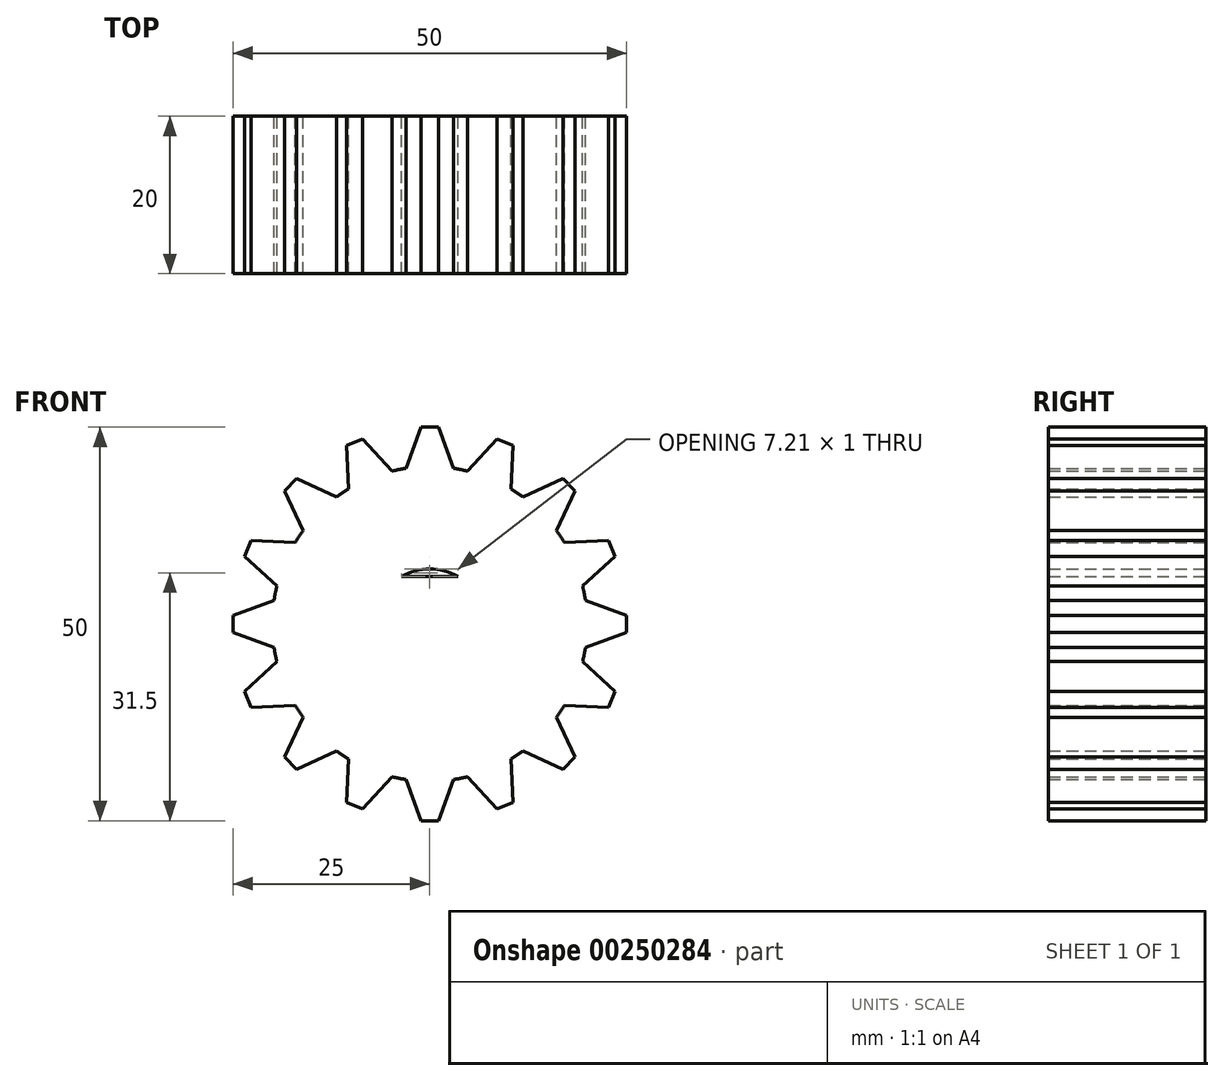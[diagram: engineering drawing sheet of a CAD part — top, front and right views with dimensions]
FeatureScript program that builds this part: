
annotation { "Feature Type Name" : "Feature", "Feature Type Description" : "" }
export const myFeature = defineFeature(function(context is Context, id is Id, definition is map)
    precondition{}
    {
        {
            var Q0;
            Q0=qCreatedBy(makeId("Front.planeOp"),FACE);
            var sketch = newSketch(context, id + "F0", { "sketchPlane" : qUnion([Q0])});
            skCircle(sketch, "E0", {"center": v(0, 0) * mm, "radius": 20 * mm});
            skPoint(sketch, "E1", {"position": v(0, 20) * mm});
            skLineSegment(sketch, "E2", {"start": v(0, 20) * mm, "end": v(0, 30) * mm, "construction": true});
            skPoint(sketch, "E3", {"position": v(0, 25) * mm});
            skLineSegment(sketch, "E4", {"start": v(-1.1, 25) * mm, "end": v(1.1, 25) * mm});
            skLineSegment(sketch, "E5", {"start": v(1.1, 25) * mm, "end": v(3, 19.77) * mm});
            skLineSegment(sketch, "E6", {"start": v(-1.1, 25) * mm, "end": v(-3, 19.77) * mm});
            skLineSegment(sketch, "E7", {"start": v(-3, 19.77) * mm, "end": v(3, 19.77) * mm});
            skLineSegment(sketch, "E8.1.0", {"start": v(-8.55, 23.52) * mm, "end": v(-4.8, 19.42) * mm});
            skLineSegment(sketch, "E8.1.1", {"start": v(-10.58, 22.68) * mm, "end": v(-10.34, 17.12) * mm});
            skPoint(sketch, "E8.1.2", {"position": v(-9.57, 23.1) * mm});
            skLineSegment(sketch, "E8.1.3", {"start": v(-10.34, 17.12) * mm, "end": v(-4.8, 19.42) * mm});
            skLineSegment(sketch, "E8.1.4", {"start": v(-7.65, 18.48) * mm, "end": v(-11.48, 27.72) * mm, "construction": true});
            skPoint(sketch, "E8.1.5", {"position": v(-7.65, 18.48) * mm});
            skLineSegment(sketch, "E8.1.6", {"start": v(-10.58, 22.68) * mm, "end": v(-8.55, 23.52) * mm});
            skLineSegment(sketch, "E8.2.0", {"start": v(-16.9, 18.45) * mm, "end": v(-11.86, 16.1) * mm});
            skLineSegment(sketch, "E8.2.1", {"start": v(-18.45, 16.9) * mm, "end": v(-16.1, 11.86) * mm});
            skPoint(sketch, "E8.2.2", {"position": v(-17.68, 17.68) * mm});
            skLineSegment(sketch, "E8.2.3", {"start": v(-16.1, 11.86) * mm, "end": v(-11.86, 16.1) * mm});
            skLineSegment(sketch, "E8.2.4", {"start": v(-14.14, 14.14) * mm, "end": v(-21.21, 21.21) * mm, "construction": true});
            skPoint(sketch, "E8.2.5", {"position": v(-14.14, 14.14) * mm});
            skLineSegment(sketch, "E8.2.6", {"start": v(-18.45, 16.9) * mm, "end": v(-16.9, 18.45) * mm});
            skLineSegment(sketch, "E8.3.0", {"start": v(-22.68, 10.58) * mm, "end": v(-17.12, 10.34) * mm});
            skLineSegment(sketch, "E8.3.1", {"start": v(-23.52, 8.55) * mm, "end": v(-19.42, 4.8) * mm});
            skPoint(sketch, "E8.3.2", {"position": v(-23.1, 9.57) * mm});
            skLineSegment(sketch, "E8.3.3", {"start": v(-19.42, 4.8) * mm, "end": v(-17.12, 10.34) * mm});
            skLineSegment(sketch, "E8.3.4", {"start": v(-18.48, 7.65) * mm, "end": v(-27.72, 11.48) * mm, "construction": true});
            skPoint(sketch, "E8.3.5", {"position": v(-18.48, 7.65) * mm});
            skLineSegment(sketch, "E8.3.6", {"start": v(-23.52, 8.55) * mm, "end": v(-22.68, 10.58) * mm});
            skLineSegment(sketch, "E8.4.0", {"start": v(-25, 1.1) * mm, "end": v(-19.77, 3) * mm});
            skLineSegment(sketch, "E8.4.1", {"start": v(-25, -1.1) * mm, "end": v(-19.77, -3) * mm});
            skPoint(sketch, "E8.4.2", {"position": v(-25, 0) * mm});
            skLineSegment(sketch, "E8.4.3", {"start": v(-19.77, -3) * mm, "end": v(-19.77, 3) * mm});
            skLineSegment(sketch, "E8.4.4", {"start": v(-20, 0) * mm, "end": v(-30, 0) * mm, "construction": true});
            skPoint(sketch, "E8.4.5", {"position": v(-20, 0) * mm});
            skLineSegment(sketch, "E8.4.6", {"start": v(-25, -1.1) * mm, "end": v(-25, 1.1) * mm});
            skLineSegment(sketch, "E8.5.0", {"start": v(-23.52, -8.55) * mm, "end": v(-19.42, -4.8) * mm});
            skLineSegment(sketch, "E8.5.1", {"start": v(-22.68, -10.58) * mm, "end": v(-17.12, -10.34) * mm});
            skPoint(sketch, "E8.5.2", {"position": v(-23.1, -9.57) * mm});
            skLineSegment(sketch, "E8.5.3", {"start": v(-17.12, -10.34) * mm, "end": v(-19.42, -4.8) * mm});
            skLineSegment(sketch, "E8.5.4", {"start": v(-18.48, -7.65) * mm, "end": v(-27.72, -11.48) * mm, "construction": true});
            skPoint(sketch, "E8.5.5", {"position": v(-18.48, -7.65) * mm});
            skLineSegment(sketch, "E8.5.6", {"start": v(-22.68, -10.58) * mm, "end": v(-23.52, -8.55) * mm});
            skLineSegment(sketch, "E8.6.0", {"start": v(-18.45, -16.9) * mm, "end": v(-16.1, -11.86) * mm});
            skLineSegment(sketch, "E8.6.1", {"start": v(-16.9, -18.45) * mm, "end": v(-11.86, -16.1) * mm});
            skPoint(sketch, "E8.6.2", {"position": v(-17.68, -17.68) * mm});
            skLineSegment(sketch, "E8.6.3", {"start": v(-11.86, -16.1) * mm, "end": v(-16.1, -11.86) * mm});
            skLineSegment(sketch, "E8.6.4", {"start": v(-14.14, -14.14) * mm, "end": v(-21.21, -21.21) * mm, "construction": true});
            skPoint(sketch, "E8.6.5", {"position": v(-14.14, -14.14) * mm});
            skLineSegment(sketch, "E8.6.6", {"start": v(-16.9, -18.45) * mm, "end": v(-18.45, -16.9) * mm});
            skLineSegment(sketch, "E8.7.0", {"start": v(-10.58, -22.68) * mm, "end": v(-10.34, -17.12) * mm});
            skLineSegment(sketch, "E8.7.1", {"start": v(-8.55, -23.52) * mm, "end": v(-4.8, -19.42) * mm});
            skPoint(sketch, "E8.7.2", {"position": v(-9.57, -23.1) * mm});
            skLineSegment(sketch, "E8.7.3", {"start": v(-4.8, -19.42) * mm, "end": v(-10.34, -17.12) * mm});
            skLineSegment(sketch, "E8.7.4", {"start": v(-7.65, -18.48) * mm, "end": v(-11.48, -27.72) * mm, "construction": true});
            skPoint(sketch, "E8.7.5", {"position": v(-7.65, -18.48) * mm});
            skLineSegment(sketch, "E8.7.6", {"start": v(-8.55, -23.52) * mm, "end": v(-10.58, -22.68) * mm});
            skLineSegment(sketch, "E8.8.0", {"start": v(-1.1, -25) * mm, "end": v(-3, -19.77) * mm});
            skLineSegment(sketch, "E8.8.1", {"start": v(1.1, -25) * mm, "end": v(3, -19.77) * mm});
            skPoint(sketch, "E8.8.2", {"position": v(0, -25) * mm});
            skLineSegment(sketch, "E8.8.3", {"start": v(3, -19.77) * mm, "end": v(-3, -19.77) * mm});
            skLineSegment(sketch, "E8.8.4", {"start": v(0, -20) * mm, "end": v(0, -30) * mm, "construction": true});
            skPoint(sketch, "E8.8.5", {"position": v(0, -20) * mm});
            skLineSegment(sketch, "E8.8.6", {"start": v(1.1, -25) * mm, "end": v(-1.1, -25) * mm});
            skLineSegment(sketch, "E8.9.0", {"start": v(8.55, -23.52) * mm, "end": v(4.8, -19.42) * mm});
            skLineSegment(sketch, "E8.9.1", {"start": v(10.58, -22.68) * mm, "end": v(10.34, -17.12) * mm});
            skPoint(sketch, "E8.9.2", {"position": v(9.57, -23.1) * mm});
            skLineSegment(sketch, "E8.9.3", {"start": v(10.34, -17.12) * mm, "end": v(4.8, -19.42) * mm});
            skLineSegment(sketch, "E8.9.4", {"start": v(7.65, -18.48) * mm, "end": v(11.48, -27.72) * mm, "construction": true});
            skPoint(sketch, "E8.9.5", {"position": v(7.65, -18.48) * mm});
            skLineSegment(sketch, "E8.9.6", {"start": v(10.58, -22.68) * mm, "end": v(8.55, -23.52) * mm});
            skLineSegment(sketch, "E8.10.0", {"start": v(16.9, -18.45) * mm, "end": v(11.86, -16.1) * mm});
            skLineSegment(sketch, "E8.10.1", {"start": v(18.45, -16.9) * mm, "end": v(16.1, -11.86) * mm});
            skPoint(sketch, "E8.10.2", {"position": v(17.68, -17.68) * mm});
            skLineSegment(sketch, "E8.10.3", {"start": v(16.1, -11.86) * mm, "end": v(11.86, -16.1) * mm});
            skLineSegment(sketch, "E8.10.4", {"start": v(14.14, -14.14) * mm, "end": v(21.21, -21.21) * mm, "construction": true});
            skPoint(sketch, "E8.10.5", {"position": v(14.14, -14.14) * mm});
            skLineSegment(sketch, "E8.10.6", {"start": v(18.45, -16.9) * mm, "end": v(16.9, -18.45) * mm});
            skLineSegment(sketch, "E8.11.0", {"start": v(22.68, -10.58) * mm, "end": v(17.12, -10.34) * mm});
            skLineSegment(sketch, "E8.11.1", {"start": v(23.52, -8.55) * mm, "end": v(19.42, -4.8) * mm});
            skPoint(sketch, "E8.11.2", {"position": v(23.1, -9.57) * mm});
            skLineSegment(sketch, "E8.11.3", {"start": v(19.42, -4.8) * mm, "end": v(17.12, -10.34) * mm});
            skLineSegment(sketch, "E8.11.4", {"start": v(18.48, -7.65) * mm, "end": v(27.72, -11.48) * mm, "construction": true});
            skPoint(sketch, "E8.11.5", {"position": v(18.48, -7.65) * mm});
            skLineSegment(sketch, "E8.11.6", {"start": v(23.52, -8.55) * mm, "end": v(22.68, -10.58) * mm});
            skLineSegment(sketch, "E8.12.0", {"start": v(25, -1.1) * mm, "end": v(19.77, -3) * mm});
            skLineSegment(sketch, "E8.12.1", {"start": v(25, 1.1) * mm, "end": v(19.77, 3) * mm});
            skPoint(sketch, "E8.12.2", {"position": v(25, 0) * mm});
            skLineSegment(sketch, "E8.12.3", {"start": v(19.77, 3) * mm, "end": v(19.77, -3) * mm});
            skLineSegment(sketch, "E8.12.4", {"start": v(20, 0) * mm, "end": v(30, 0) * mm, "construction": true});
            skPoint(sketch, "E8.12.5", {"position": v(20, 0) * mm});
            skLineSegment(sketch, "E8.12.6", {"start": v(25, 1.1) * mm, "end": v(25, -1.1) * mm});
            skLineSegment(sketch, "E8.13.0", {"start": v(23.52, 8.55) * mm, "end": v(19.42, 4.8) * mm});
            skLineSegment(sketch, "E8.13.1", {"start": v(22.68, 10.58) * mm, "end": v(17.12, 10.34) * mm});
            skPoint(sketch, "E8.13.2", {"position": v(23.1, 9.57) * mm});
            skLineSegment(sketch, "E8.13.3", {"start": v(17.12, 10.34) * mm, "end": v(19.42, 4.8) * mm});
            skLineSegment(sketch, "E8.13.4", {"start": v(18.48, 7.65) * mm, "end": v(27.72, 11.48) * mm, "construction": true});
            skPoint(sketch, "E8.13.5", {"position": v(18.48, 7.65) * mm});
            skLineSegment(sketch, "E8.13.6", {"start": v(22.68, 10.58) * mm, "end": v(23.52, 8.55) * mm});
            skLineSegment(sketch, "E8.14.0", {"start": v(18.45, 16.9) * mm, "end": v(16.1, 11.86) * mm});
            skLineSegment(sketch, "E8.14.1", {"start": v(16.9, 18.45) * mm, "end": v(11.86, 16.1) * mm});
            skPoint(sketch, "E8.14.2", {"position": v(17.68, 17.68) * mm});
            skLineSegment(sketch, "E8.14.3", {"start": v(11.86, 16.1) * mm, "end": v(16.1, 11.86) * mm});
            skLineSegment(sketch, "E8.14.4", {"start": v(14.14, 14.14) * mm, "end": v(21.21, 21.21) * mm, "construction": true});
            skPoint(sketch, "E8.14.5", {"position": v(14.14, 14.14) * mm});
            skLineSegment(sketch, "E8.14.6", {"start": v(16.9, 18.45) * mm, "end": v(18.45, 16.9) * mm});
            skLineSegment(sketch, "E8.15.0", {"start": v(10.58, 22.68) * mm, "end": v(10.34, 17.12) * mm});
            skLineSegment(sketch, "E8.15.1", {"start": v(8.55, 23.52) * mm, "end": v(4.8, 19.42) * mm});
            skPoint(sketch, "E8.15.2", {"position": v(9.57, 23.1) * mm});
            skLineSegment(sketch, "E8.15.3", {"start": v(4.8, 19.42) * mm, "end": v(10.34, 17.12) * mm});
            skLineSegment(sketch, "E8.15.4", {"start": v(7.65, 18.48) * mm, "end": v(11.48, 27.72) * mm, "construction": true});
            skPoint(sketch, "E8.15.5", {"position": v(7.65, 18.48) * mm});
            skLineSegment(sketch, "E8.15.6", {"start": v(8.55, 23.52) * mm, "end": v(10.58, 22.68) * mm});
            skSolve(sketch);
        }
        {
            var Q0;
            Q0 = qSketchRegion(id + "F0", true);
            extrude(context, id + "F1", {"entities" : qUnion([Q0]), "depth" : 20 * mm});
        }
        {
            var Q0;
            Q0=makeQuery(id+"F1.opExtrude","CAP_FACE",FACE,{"disambiguationData":[OSD([sQuery(id+"F0.wireOp",EDGE,"E4"),sQuery(id+"F0.wireOp",EDGE,"E5"),sQuery(id+"F0.wireOp",EDGE,"E6"),sQuery(id+"F0.wireOp",EDGE,"17c51863-979c-42ed-b14d-551197cb4550.1.4"),sQuery(id+"F0.wireOp",EDGE,"17c51863-979c-42ed-b14d-551197cb4550.1.5"),sQuery(id+"F0.wireOp",EDGE,"17c51863-979c-42ed-b14d-551197cb4550.1.6"),sQuery(id+"F0.wireOp",EDGE,"17c51863-979c-42ed-b14d-551197cb4550.2.4"),sQuery(id+"F0.wireOp",EDGE,"17c51863-979c-42ed-b14d-551197cb4550.2.5"),sQuery(id+"F0.wireOp",EDGE,"17c51863-979c-42ed-b14d-551197cb4550.2.6"),sQuery(id+"F0.wireOp",EDGE,"17c51863-979c-42ed-b14d-551197cb4550.3.4"),sQuery(id+"F0.wireOp",EDGE,"17c51863-979c-42ed-b14d-551197cb4550.3.5"),sQuery(id+"F0.wireOp",EDGE,"17c51863-979c-42ed-b14d-551197cb4550.3.6"),sQuery(id+"F0.wireOp",EDGE,"17c51863-979c-42ed-b14d-551197cb4550.4.4"),sQuery(id+"F0.wireOp",EDGE,"17c51863-979c-42ed-b14d-551197cb4550.4.5"),sQuery(id+"F0.wireOp",EDGE,"17c51863-979c-42ed-b14d-551197cb4550.4.6"),sQuery(id+"F0.wireOp",EDGE,"17c51863-979c-42ed-b14d-551197cb4550.5.4"),sQuery(id+"F0.wireOp",EDGE,"17c51863-979c-42ed-b14d-551197cb4550.5.5"),sQuery(id+"F0.wireOp",EDGE,"17c51863-979c-42ed-b14d-551197cb4550.5.6"),sQuery(id+"F0.wireOp",EDGE,"17c51863-979c-42ed-b14d-551197cb4550.6.4"),sQuery(id+"F0.wireOp",EDGE,"17c51863-979c-42ed-b14d-551197cb4550.6.5"),sQuery(id+"F0.wireOp",EDGE,"17c51863-979c-42ed-b14d-551197cb4550.6.6"),sQuery(id+"F0.wireOp",EDGE,"17c51863-979c-42ed-b14d-551197cb4550.7.4"),sQuery(id+"F0.wireOp",EDGE,"17c51863-979c-42ed-b14d-551197cb4550.7.5"),sQuery(id+"F0.wireOp",EDGE,"17c51863-979c-42ed-b14d-551197cb4550.7.6"),sQuery(id+"F0.wireOp",EDGE,"17c51863-979c-42ed-b14d-551197cb4550.8.4"),sQuery(id+"F0.wireOp",EDGE,"17c51863-979c-42ed-b14d-551197cb4550.8.5"),sQuery(id+"F0.wireOp",EDGE,"17c51863-979c-42ed-b14d-551197cb4550.8.6"),sQuery(id+"F0.wireOp",EDGE,"17c51863-979c-42ed-b14d-551197cb4550.9.4"),sQuery(id+"F0.wireOp",EDGE,"17c51863-979c-42ed-b14d-551197cb4550.9.5"),sQuery(id+"F0.wireOp",EDGE,"17c51863-979c-42ed-b14d-551197cb4550.9.6"),sQuery(id+"F0.wireOp",EDGE,"17c51863-979c-42ed-b14d-551197cb4550.10.4"),sQuery(id+"F0.wireOp",EDGE,"17c51863-979c-42ed-b14d-551197cb4550.10.5"),sQuery(id+"F0.wireOp",EDGE,"17c51863-979c-42ed-b14d-551197cb4550.10.6"),sQuery(id+"F0.wireOp",EDGE,"17c51863-979c-42ed-b14d-551197cb4550.11.4"),sQuery(id+"F0.wireOp",EDGE,"17c51863-979c-42ed-b14d-551197cb4550.11.5"),sQuery(id+"F0.wireOp",EDGE,"17c51863-979c-42ed-b14d-551197cb4550.11.6"),sQuery(id+"F0.wireOp",EDGE,"17c51863-979c-42ed-b14d-551197cb4550.12.4"),sQuery(id+"F0.wireOp",EDGE,"17c51863-979c-42ed-b14d-551197cb4550.12.5"),sQuery(id+"F0.wireOp",EDGE,"17c51863-979c-42ed-b14d-551197cb4550.12.6"),sQuery(id+"F0.wireOp",EDGE,"17c51863-979c-42ed-b14d-551197cb4550.13.4"),sQuery(id+"F0.wireOp",EDGE,"17c51863-979c-42ed-b14d-551197cb4550.13.5"),sQuery(id+"F0.wireOp",EDGE,"17c51863-979c-42ed-b14d-551197cb4550.13.6"),sQuery(id+"F0.wireOp",EDGE,"17c51863-979c-42ed-b14d-551197cb4550.14.4"),sQuery(id+"F0.wireOp",EDGE,"17c51863-979c-42ed-b14d-551197cb4550.14.5"),sQuery(id+"F0.wireOp",EDGE,"17c51863-979c-42ed-b14d-551197cb4550.14.6"),sQuery(id+"F0.wireOp",EDGE,"17c51863-979c-42ed-b14d-551197cb4550.15.4"),sQuery(id+"F0.wireOp",EDGE,"17c51863-979c-42ed-b14d-551197cb4550.15.5"),sQuery(id+"F0.wireOp",EDGE,"17c51863-979c-42ed-b14d-551197cb4550.15.6"),sQuery(id+"F0.wireOp",EDGE,"17c51863-979c-42ed-b14d-551197cb4550.16.4"),sQuery(id+"F0.wireOp",EDGE,"17c51863-979c-42ed-b14d-551197cb4550.16.5"),sQuery(id+"F0.wireOp",EDGE,"17c51863-979c-42ed-b14d-551197cb4550.16.6"),sQuery(id+"F0.wireOp",EDGE,"17c51863-979c-42ed-b14d-551197cb4550.17.4"),sQuery(id+"F0.wireOp",EDGE,"17c51863-979c-42ed-b14d-551197cb4550.17.5"),sQuery(id+"F0.wireOp",EDGE,"17c51863-979c-42ed-b14d-551197cb4550.17.6"),sQuery(id+"F0.wireOp",EDGE,"17c51863-979c-42ed-b14d-551197cb4550.18.4"),sQuery(id+"F0.wireOp",EDGE,"17c51863-979c-42ed-b14d-551197cb4550.18.5"),sQuery(id+"F0.wireOp",EDGE,"17c51863-979c-42ed-b14d-551197cb4550.18.6"),sQuery(id+"F0.wireOp",EDGE,"17c51863-979c-42ed-b14d-551197cb4550.19.4"),sQuery(id+"F0.wireOp",EDGE,"17c51863-979c-42ed-b14d-551197cb4550.19.5"),sQuery(id+"F0.wireOp",EDGE,"17c51863-979c-42ed-b14d-551197cb4550.19.6"),sQuery(id+"F0.wireOp",EDGE,"17c51863-979c-42ed-b14d-551197cb4550.20.4"),sQuery(id+"F0.wireOp",EDGE,"17c51863-979c-42ed-b14d-551197cb4550.20.5"),sQuery(id+"F0.wireOp",EDGE,"17c51863-979c-42ed-b14d-551197cb4550.20.6"),sQuery(id+"F0.wireOp",EDGE,"17c51863-979c-42ed-b14d-551197cb4550.21.4"),sQuery(id+"F0.wireOp",EDGE,"17c51863-979c-42ed-b14d-551197cb4550.21.5"),sQuery(id+"F0.wireOp",EDGE,"17c51863-979c-42ed-b14d-551197cb4550.21.6"),sQuery(id+"F0.wireOp",EDGE,"17c51863-979c-42ed-b14d-551197cb4550.22.4"),sQuery(id+"F0.wireOp",EDGE,"17c51863-979c-42ed-b14d-551197cb4550.22.5"),sQuery(id+"F0.wireOp",EDGE,"17c51863-979c-42ed-b14d-551197cb4550.22.6"),sQuery(id+"F0.wireOp",EDGE,"17c51863-979c-42ed-b14d-551197cb4550.23.4"),sQuery(id+"F0.wireOp",EDGE,"17c51863-979c-42ed-b14d-551197cb4550.23.5"),sQuery(id+"F0.wireOp",EDGE,"17c51863-979c-42ed-b14d-551197cb4550.23.6"),sQuery(id+"F0.wireOp",EDGE,"17c51863-979c-42ed-b14d-551197cb4550.24.4"),sQuery(id+"F0.wireOp",EDGE,"17c51863-979c-42ed-b14d-551197cb4550.24.5"),sQuery(id+"F0.wireOp",EDGE,"17c51863-979c-42ed-b14d-551197cb4550.24.6"),sQuery(id+"F0.wireOp",EDGE,"17c51863-979c-42ed-b14d-551197cb4550.25.4"),sQuery(id+"F0.wireOp",EDGE,"17c51863-979c-42ed-b14d-551197cb4550.25.5"),sQuery(id+"F0.wireOp",EDGE,"17c51863-979c-42ed-b14d-551197cb4550.25.6"),sQuery(id+"F0.wireOp",EDGE,"17c51863-979c-42ed-b14d-551197cb4550.26.4"),sQuery(id+"F0.wireOp",EDGE,"17c51863-979c-42ed-b14d-551197cb4550.26.5"),sQuery(id+"F0.wireOp",EDGE,"17c51863-979c-42ed-b14d-551197cb4550.26.6"),sQuery(id+"F0.wireOp",EDGE,"17c51863-979c-42ed-b14d-551197cb4550.27.4"),sQuery(id+"F0.wireOp",EDGE,"17c51863-979c-42ed-b14d-551197cb4550.27.5"),sQuery(id+"F0.wireOp",EDGE,"17c51863-979c-42ed-b14d-551197cb4550.27.6"),sQuery(id+"F0.wireOp",EDGE,"17c51863-979c-42ed-b14d-551197cb4550.27.7")])],"isStart":true});
            var sketch = newSketch(context, id + "F2", { "sketchPlane" : qUnion([Q0])});
            skCircle(sketch, "E9", {"center": v(0, 0) * mm, "radius": 7 * mm});
            skLineSegment(sketch, "E10", {"start": v(-15.72, 6) * mm, "end": v(6, 6) * mm});
            skLineSegment(sketch, "E11", {"start": v(6, -12.05) * mm, "end": v(6, 6) * mm});
            skLineSegment(sketch, "E12", {"start": v(-15.72, 6) * mm, "end": v(-15.72, 12.76) * mm});
            skLineSegment(sketch, "E13", {"start": v(-15.72, 12.76) * mm, "end": v(13.2, 12.76) * mm});
            skLineSegment(sketch, "E14", {"start": v(13.2, 12.76) * mm, "end": v(13.2, -12.47) * mm});
            skLineSegment(sketch, "E15", {"start": v(13.2, -12.47) * mm, "end": v(6, -12.05) * mm});
            skSolve(sketch);
        }
        {
            var Q0;
            {var subQ0=sQuery(id+"F2.wireOp",EDGE,"E10");var subQ1=sQuery(id+"F2.wireOp",EDGE,"E9");var subQ2=makeQuery(id+"F2.imprint","INTERSECT",VERTEX,{"disambiguationData":[OD(0.0)],"derivedFrom":[subQ1,subQ0]});Q0=makeQuery(id+"F2.imprint","IMPRINT",FACE,{"disambiguationData":[TD([[makeQuery(id+"F2.imprint","IMPRINT",EDGE,{"disambiguationData":[TD([[subQ2,1.0]])],"derivedFrom":subQ1}),1.0]])]});}
            extrude(context, id + "F3", {"entities" : qUnion([Q0]), "operationType" : NewBodyOperationType.REMOVE, "oppositeDirection" : true, "depth" : 25 * mm});
        }
    });
